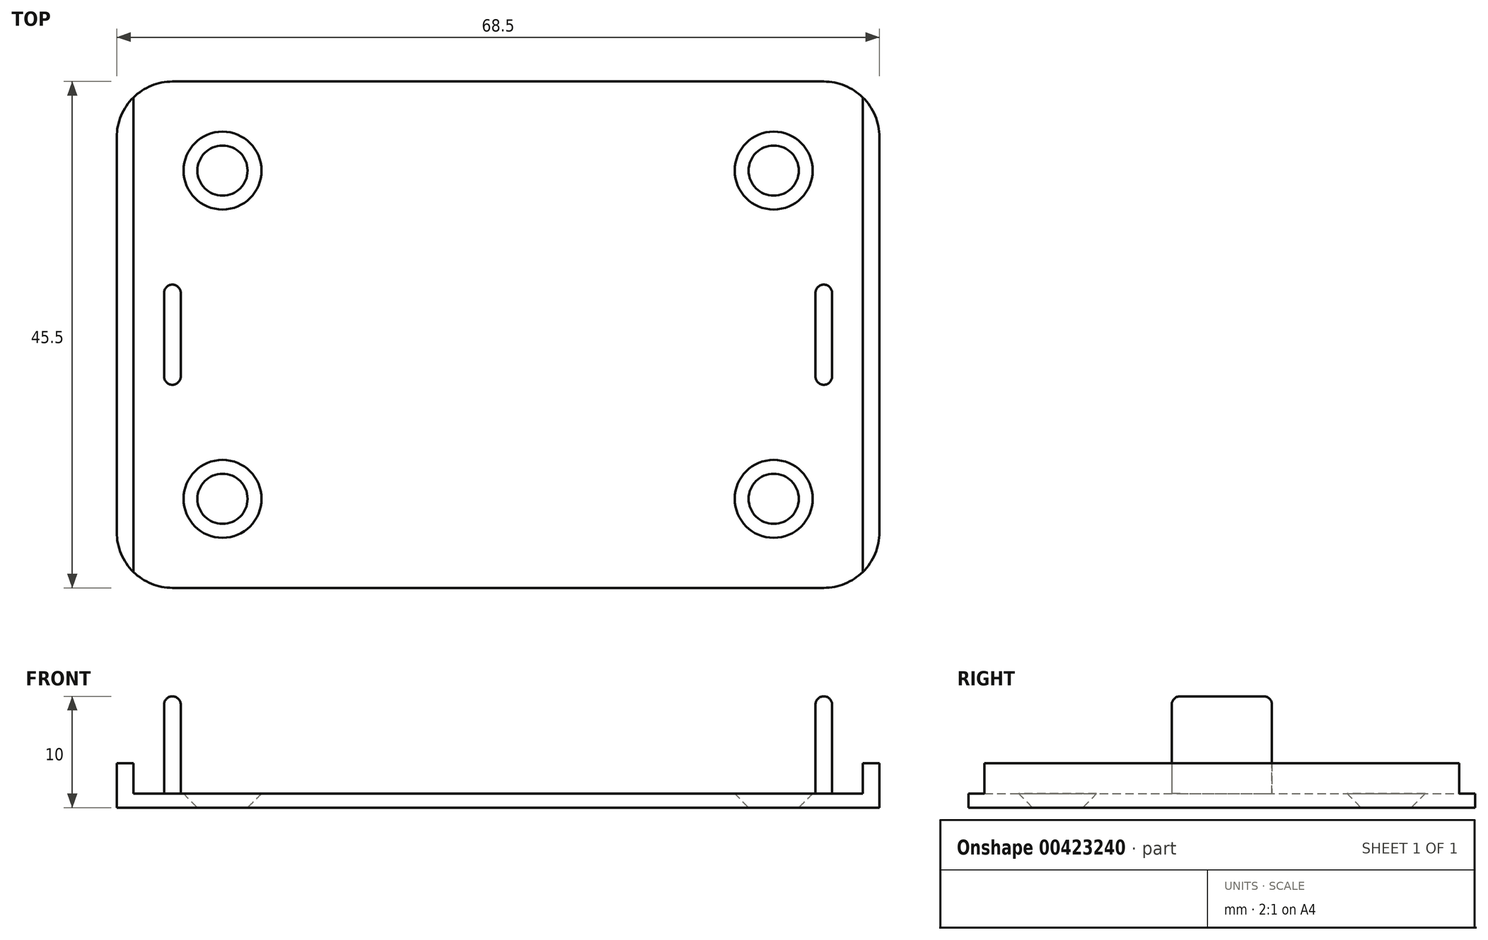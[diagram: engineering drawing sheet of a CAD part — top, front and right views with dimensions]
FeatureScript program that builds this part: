
annotation { "Feature Type Name" : "Feature", "Feature Type Description" : "" }
export const myFeature = defineFeature(function(context is Context, id is Id, definition is map)
    precondition{}
    {
        {
            var Q0;
            Q0=qCreatedBy(makeId("Top.planeOp"),FACE);
            var sketch = newSketch(context, id + "F0", { "sketchPlane" : qUnion([Q0])});
            skLineSegment(sketch, "E0.bottom", {"start": v(32.75, -22.75) * mm, "end": v(-32.75, -22.75) * mm});
            skLineSegment(sketch, "E0.top", {"start": v(32.75, 22.75) * mm, "end": v(-32.75, 22.75) * mm});
            skLineSegment(sketch, "E0.left", {"start": v(32.75, -22.75) * mm, "end": v(32.75, 22.75) * mm});
            skLineSegment(sketch, "E0.right", {"start": v(-32.75, -22.75) * mm, "end": v(-32.75, 22.75) * mm});
            skPoint(sketch, "E0.middle", {"position": v(0, 0) * mm});
            skLineSegment(sketch, "E1.bottom", {"start": v(-28.5, -4.5) * mm, "end": v(-30, -4.5) * mm});
            skLineSegment(sketch, "E1.top", {"start": v(-28.5, 4.5) * mm, "end": v(-30, 4.5) * mm});
            skLineSegment(sketch, "E1.left", {"start": v(-28.5, -4.5) * mm, "end": v(-28.5, 4.5) * mm});
            skLineSegment(sketch, "E1.right", {"start": v(-30, -4.5) * mm, "end": v(-30, 4.5) * mm});
            skPoint(sketch, "E1.middle", {"position": v(-29.25, 0) * mm});
            skLineSegment(sketch, "E2.bottom", {"start": v(30, -4.5) * mm, "end": v(28.5, -4.5) * mm});
            skLineSegment(sketch, "E2.top", {"start": v(30, 4.5) * mm, "end": v(28.5, 4.5) * mm});
            skLineSegment(sketch, "E2.left", {"start": v(30, -4.5) * mm, "end": v(30, 4.5) * mm});
            skLineSegment(sketch, "E2.right", {"start": v(28.5, -4.5) * mm, "end": v(28.5, 4.5) * mm});
            skPoint(sketch, "E2.middle", {"position": v(29.25, 0) * mm});
            skCircle(sketch, "E3", {"center": v(24.75, -14.75) * mm, "radius": 1.5 * mm});
            skCircle(sketch, "E4", {"center": v(24.75, 14.75) * mm, "radius": 1.5 * mm});
            skCircle(sketch, "E5", {"center": v(-24.75, 14.75) * mm, "radius": 1.5 * mm});
            skCircle(sketch, "E6", {"center": v(-24.75, -14.75) * mm, "radius": 1.5 * mm});
            skLineSegment(sketch, "E7.0", {"start": v(34.25, -22.75) * mm, "end": v(34.25, 22.75) * mm});
            skLineSegment(sketch, "E8.0", {"start": v(-34.25, -22.75) * mm, "end": v(-34.25, 22.75) * mm});
            skLineSegment(sketch, "E9", {"start": v(-34.25, 22.75) * mm, "end": v(-32.75, 22.75) * mm});
            skLineSegment(sketch, "E10", {"start": v(-34.25, -22.75) * mm, "end": v(-32.75, -22.75) * mm});
            skLineSegment(sketch, "E11", {"start": v(32.75, 22.75) * mm, "end": v(34.25, 22.75) * mm});
            skLineSegment(sketch, "E12", {"start": v(32.75, -22.75) * mm, "end": v(34.25, -22.75) * mm});
            skSolve(sketch);
        }
        {
            var Q0;
            Q0=makeQuery(id+"F0.imprint","IMPRINT",FACE,{"disambiguationData":[TD([[makeQuery(id+"F0.imprint","IMPRINT",EDGE,{"derivedFrom":sQuery(id+"F0.wireOp",EDGE,"E0.bottom")}),-1.0]])]});
            extrude(context, id + "F1", {"entities" : qUnion([Q0]), "depth" : 1.25 * mm});
        }
        {
            var Q0;
            Q0=makeQuery(id+"F0.imprint","IMPRINT",FACE,{"disambiguationData":[TD([[makeQuery(id+"F0.imprint","IMPRINT",EDGE,{"derivedFrom":sQuery(id+"F0.wireOp",EDGE,"E1.bottom")}),-1.0]])]});
            var Q1;
            Q1=makeQuery(id+"F0.imprint","IMPRINT",FACE,{"disambiguationData":[TD([[makeQuery(id+"F0.imprint","IMPRINT",EDGE,{"derivedFrom":sQuery(id+"F0.wireOp",EDGE,"E2.bottom")}),-1.0]])]});
            extrude(context, id + "F2", {"entities" : qUnion([Q0, Q1]), "operationType" : NewBodyOperationType.ADD, "depth" : 10 * mm});
        }
        {
            var Q0;
            Q0=makeQuery(id+"F0.imprint","IMPRINT",FACE,{"disambiguationData":[TD([[makeQuery(id+"F0.imprint","IMPRINT",EDGE,{"derivedFrom":sQuery(id+"F0.wireOp",EDGE,"E0.right")}),1.0]])]});
            var Q1;
            Q1=makeQuery(id+"F0.imprint","IMPRINT",FACE,{"disambiguationData":[TD([[makeQuery(id+"F0.imprint","IMPRINT",EDGE,{"derivedFrom":sQuery(id+"F0.wireOp",EDGE,"E0.left")}),-1.0]])]});
            extrude(context, id + "F3", {"entities" : qUnion([Q0, Q1]), "operationType" : NewBodyOperationType.ADD, "depth" : 4 * mm});
        }
        {
            var Q0;
            Q0=makeQuery(id+"F1.opExtrude","CAP_EDGE",EDGE,{"disambiguationData":[OSD([sQuery(id+"F0.wireOp",EDGE,"E5")])],"isStart":false});
            var Q1;
            Q1=makeQuery(id+"F1.opExtrude","CAP_EDGE",EDGE,{"disambiguationData":[OSD([sQuery(id+"F0.wireOp",EDGE,"E6")])],"isStart":false});
            var Q2;
            Q2=makeQuery(id+"F1.opExtrude","CAP_EDGE",EDGE,{"disambiguationData":[OSD([sQuery(id+"F0.wireOp",EDGE,"E4")])],"isStart":false});
            var Q3;
            Q3=makeQuery(id+"F1.opExtrude","CAP_EDGE",EDGE,{"disambiguationData":[OSD([sQuery(id+"F0.wireOp",EDGE,"E3")])],"isStart":false});
            chamfer(context, id + "F4", {"entities" : qUnion([Q0, Q1, Q2, Q3]), "width" : 2 * mm, "tangentPropagation" : true});
        }
        {
            var Q0;
            Q0=makeQuery(id+"F2.opExtrude","SWEPT_EDGE",EDGE,{"disambiguationData":[OSD([sQuery(id+"F0.wireOp",EDGE,"E1.top"),sQuery(id+"F0.wireOp",EDGE,"E1.right")])]});
            var Q1;
            Q1=makeQuery(id+"F2.opExtrude","SWEPT_EDGE",EDGE,{"disambiguationData":[OSD([sQuery(id+"F0.wireOp",EDGE,"E2.top"),sQuery(id+"F0.wireOp",EDGE,"E2.left")])]});
            var Q2;
            Q2=makeQuery(id+"F2.opExtrude","SWEPT_EDGE",EDGE,{"disambiguationData":[OSD([sQuery(id+"F0.wireOp",EDGE,"E2.top"),sQuery(id+"F0.wireOp",EDGE,"E2.right")])]});
            var Q3;
            Q3=makeQuery(id+"F2.opExtrude","SWEPT_EDGE",EDGE,{"disambiguationData":[OSD([sQuery(id+"F0.wireOp",EDGE,"E1.bottom"),sQuery(id+"F0.wireOp",EDGE,"E1.right")])]});
            var Q4;
            Q4=makeQuery(id+"F2.opExtrude","SWEPT_EDGE",EDGE,{"disambiguationData":[OSD([sQuery(id+"F0.wireOp",EDGE,"E1.bottom"),sQuery(id+"F0.wireOp",EDGE,"E1.left")])]});
            var Q5;
            Q5=makeQuery(id+"F2.opExtrude","SWEPT_EDGE",EDGE,{"disambiguationData":[OSD([sQuery(id+"F0.wireOp",EDGE,"E2.bottom"),sQuery(id+"F0.wireOp",EDGE,"E2.right")])]});
            var Q6;
            Q6=makeQuery(id+"F2.opExtrude","SWEPT_EDGE",EDGE,{"disambiguationData":[OSD([sQuery(id+"F0.wireOp",EDGE,"E2.bottom"),sQuery(id+"F0.wireOp",EDGE,"E2.left")])]});
            var Q7;
            Q7=makeQuery(id+"F2.opExtrude","SWEPT_EDGE",EDGE,{"disambiguationData":[OSD([sQuery(id+"F0.wireOp",EDGE,"E1.top"),sQuery(id+"F0.wireOp",EDGE,"E1.left")])]});
            fillet(context, id + "F5", {"entities" : qUnion([Q0, Q1, Q2, Q3, Q4, Q5, Q6, Q7]), "radius" : .75 * mm, "tangentPropagation" : true, "allowEdgeOverflow" : false});
        }
        {
            var Q0;
            Q0=makeQuery(id+"F2.opExtrude","CAP_FACE",FACE,{"disambiguationData":[OSD([sQuery(id+"F0.wireOp",EDGE,"E1.bottom"),sQuery(id+"F0.wireOp",EDGE,"E1.top"),sQuery(id+"F0.wireOp",EDGE,"E1.left"),sQuery(id+"F0.wireOp",EDGE,"E1.right")])],"isStart":false});
            var Q1;
            Q1=makeQuery(id+"F2.opExtrude","CAP_FACE",FACE,{"disambiguationData":[OSD([sQuery(id+"F0.wireOp",EDGE,"E2.bottom"),sQuery(id+"F0.wireOp",EDGE,"E2.top"),sQuery(id+"F0.wireOp",EDGE,"E2.left"),sQuery(id+"F0.wireOp",EDGE,"E2.right")])],"isStart":false});
            fillet(context, id + "F6", {"entities" : qUnion([Q0, Q1]), "radius" : .75 * mm, "tangentPropagation" : true, "allowEdgeOverflow" : false});
        }
        {
            var Q0;
            Q0=makeQuery(id+"F3.opExtrude","SWEPT_EDGE",EDGE,{"disambiguationData":[OSD([sQuery(id+"F0.wireOp",EDGE,"E8.0"),sQuery(id+"F0.wireOp",EDGE,"E10")])]});
            var Q1;
            Q1=makeQuery(id+"F3.opExtrude","SWEPT_EDGE",EDGE,{"disambiguationData":[OSD([sQuery(id+"F0.wireOp",EDGE,"E7.0"),sQuery(id+"F0.wireOp",EDGE,"E12")])]});
            var Q2;
            Q2=makeQuery(id+"F3.opExtrude","SWEPT_EDGE",EDGE,{"disambiguationData":[OSD([sQuery(id+"F0.wireOp",EDGE,"E7.0"),sQuery(id+"F0.wireOp",EDGE,"E11")])]});
            var Q3;
            Q3=makeQuery(id+"F3.opExtrude","SWEPT_EDGE",EDGE,{"disambiguationData":[OSD([sQuery(id+"F0.wireOp",EDGE,"E8.0"),sQuery(id+"F0.wireOp",EDGE,"E9")])]});
            fillet(context, id + "F7", {"entities" : qUnion([Q0, Q1, Q2, Q3]), "radius" : 5 * mm, "tangentPropagation" : true, "allowEdgeOverflow" : false});
        }
    });
